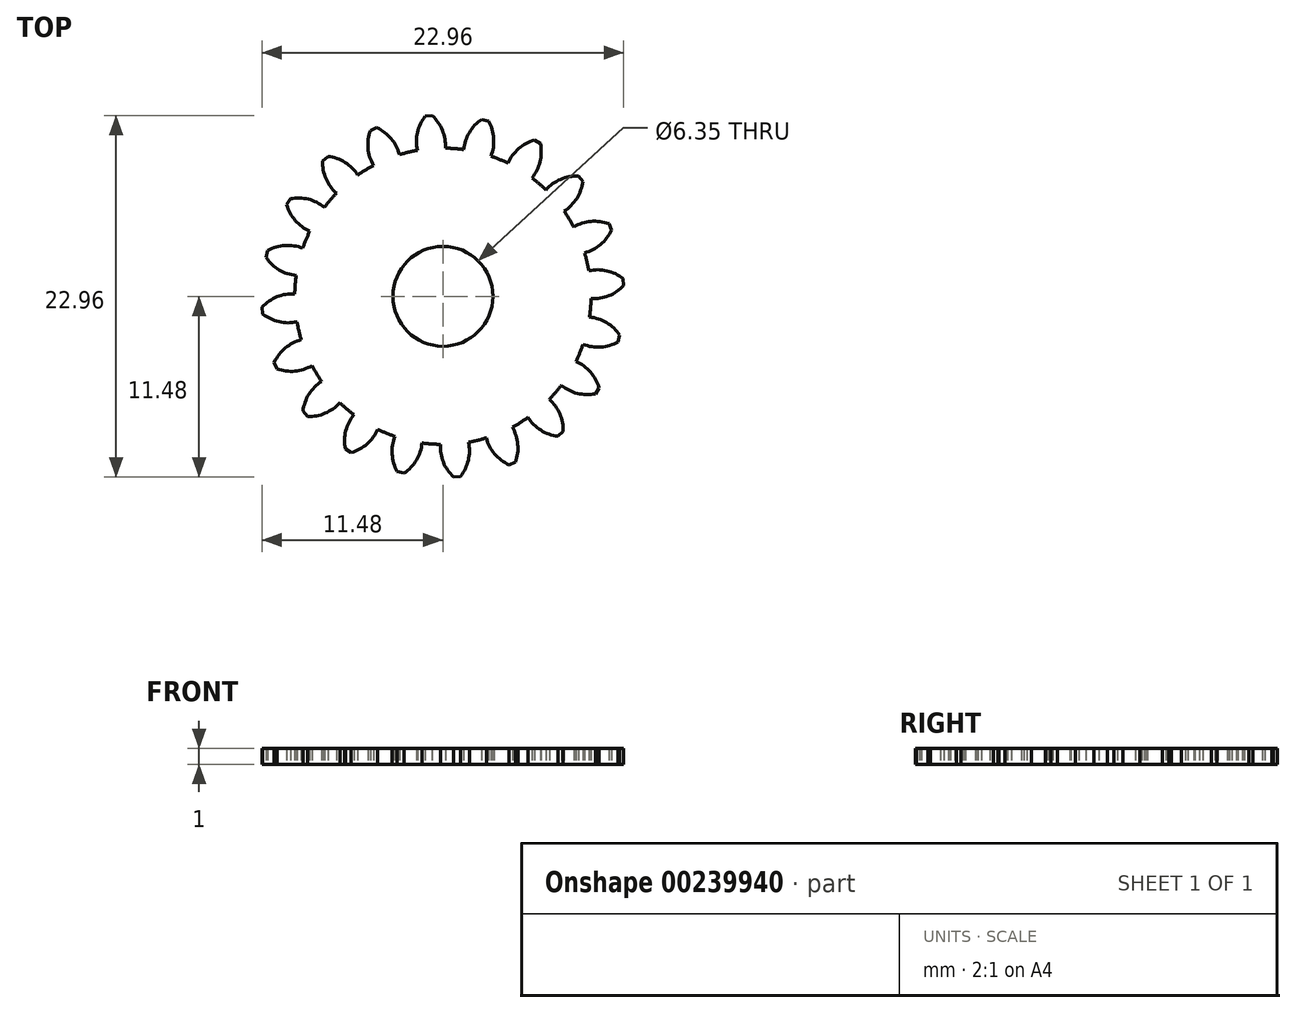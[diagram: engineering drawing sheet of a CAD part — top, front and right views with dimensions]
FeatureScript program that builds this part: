
annotation { "Feature Type Name" : "Feature", "Feature Type Description" : "" }
export const myFeature = defineFeature(function(context is Context, id is Id, definition is map)
    precondition{}
    {
        {
            assignVariable(context, id + "F0", {"name" : "GearDepth", "anyValue" : 1});
        }
        {
            var Q0;
            Q0=qCreatedBy(makeId("Top.planeOp"),FACE);
            var sketch = newSketch(context, id + "F1", { "sketchPlane" : qUnion([Q0])});
            skCircle(sketch, "E0", {"center": v(0, 0) * mm, "radius": 9.4 * mm});
            skCircle(sketch, "E1", {"center": v(0, 0) * mm, "radius": 10.45 * mm, "construction": true});
            skCircle(sketch, "E2", {"center": v(0, 0) * mm, "radius": 11.5 * mm, "construction": true});
            skLineSegment(sketch, "E3", {"start": v(0, 0) * mm, "end": v(0, 17.6) * mm, "construction": true});
            skLineSegment(sketch, "E4", {"start": v(0, 0) * mm, "end": v(-1.42, 18) * mm, "construction": true});
            skLineSegment(sketch, "E5", {"start": v(0, 10.45) * mm, "end": v(-10.54, 10.45) * mm, "construction": true});
            skLineSegment(sketch, "E6", {"start": v(0, 10.45) * mm, "end": v(-10.3, 6.7) * mm, "construction": true});
            skCircle(sketch, "E7", {"center": v(0, 10.45) * mm, "radius": 2.61 * mm, "construction": true});
            skCircle(sketch, "E8", {"center": v(-2.46, 9.56) * mm, "radius": 2.61 * mm, "construction": true});
            skArc(sketch, "E9", {"start": v(-4.91, 10.45) * mm, "mid": v(-4.92, 10.42) * mm, "end": v(-4.94, 10.39) * mm});
            skArc(sketch, "E10.trimOffspring", {"start": v(0.15, 9.4) * mm, "mid": v(-0.03, 10.54) * mm, "end": v(-0.68, 11.48) * mm});
            skArc(sketch, "E11.MirrorCS", {"start": v(-1.62, 9.27) * mm, "mid": v(-1.62, 10.41) * mm, "end": v(-1.12, 11.45) * mm});
            skLineSegment(sketch, "E12", {"start": v(-1.12, 11.45) * mm, "end": v(-0.68, 11.48) * mm});
            skArc(sketch, "E13.1.0", {"start": v(-2.76, 9) * mm, "mid": v(-3.29, 10.01) * mm, "end": v(-4.2, 10.7) * mm});
            skLineSegment(sketch, "E13.1.1", {"start": v(-4.6, 10.54) * mm, "end": v(-4.2, 10.7) * mm});
            skArc(sketch, "E13.1.2", {"start": v(-4.4, 8.31) * mm, "mid": v(-4.76, 9.4) * mm, "end": v(-4.6, 10.54) * mm});
            skArc(sketch, "E13.2.0", {"start": v(-5.4, 7.7) * mm, "mid": v(-6.22, 8.5) * mm, "end": v(-7.3, 8.89) * mm});
            skLineSegment(sketch, "E13.2.1", {"start": v(-7.64, 8.6) * mm, "end": v(-7.3, 8.89) * mm});
            skArc(sketch, "E13.2.2", {"start": v(-6.76, 6.54) * mm, "mid": v(-7.43, 7.47) * mm, "end": v(-7.64, 8.6) * mm});
            skArc(sketch, "E13.3.0", {"start": v(-7.52, 5.65) * mm, "mid": v(-8.54, 6.17) * mm, "end": v(-9.69, 6.2) * mm});
            skLineSegment(sketch, "E13.3.1", {"start": v(-9.92, 5.82) * mm, "end": v(-9.69, 6.2) * mm});
            skArc(sketch, "E13.3.2", {"start": v(-8.45, 4.13) * mm, "mid": v(-9.37, 4.81) * mm, "end": v(-9.92, 5.82) * mm});
            skArc(sketch, "E13.4.0", {"start": v(-8.9, 3.05) * mm, "mid": v(-10.03, 3.23) * mm, "end": v(-11.13, 2.9) * mm});
            skLineSegment(sketch, "E13.4.1", {"start": v(-11.23, 2.47) * mm, "end": v(-11.13, 2.9) * mm});
            skArc(sketch, "E13.4.2", {"start": v(-9.32, 1.32) * mm, "mid": v(-10.4, 1.68) * mm, "end": v(-11.23, 2.47) * mm});
            skArc(sketch, "E13.5.0", {"start": v(-9.4, 0.15) * mm, "mid": v(-10.54, -0.03) * mm, "end": v(-11.48, -0.68) * mm});
            skLineSegment(sketch, "E13.5.1", {"start": v(-11.45, -1.12) * mm, "end": v(-11.48, -0.68) * mm});
            skArc(sketch, "E13.5.2", {"start": v(-9.27, -1.62) * mm, "mid": v(-10.41, -1.62) * mm, "end": v(-11.45, -1.12) * mm});
            skArc(sketch, "E13.6.0", {"start": v(-9, -2.76) * mm, "mid": v(-10.01, -3.29) * mm, "end": v(-10.7, -4.2) * mm});
            skLineSegment(sketch, "E13.6.1", {"start": v(-10.54, -4.6) * mm, "end": v(-10.7, -4.2) * mm});
            skArc(sketch, "E13.6.2", {"start": v(-8.31, -4.4) * mm, "mid": v(-9.4, -4.76) * mm, "end": v(-10.54, -4.6) * mm});
            skArc(sketch, "E13.7.0", {"start": v(-7.7, -5.4) * mm, "mid": v(-8.5, -6.22) * mm, "end": v(-8.89, -7.3) * mm});
            skLineSegment(sketch, "E13.7.1", {"start": v(-8.6, -7.64) * mm, "end": v(-8.89, -7.3) * mm});
            skArc(sketch, "E13.7.2", {"start": v(-6.54, -6.76) * mm, "mid": v(-7.47, -7.43) * mm, "end": v(-8.6, -7.64) * mm});
            skArc(sketch, "E13.8.0", {"start": v(-5.65, -7.52) * mm, "mid": v(-6.17, -8.54) * mm, "end": v(-6.2, -9.69) * mm});
            skLineSegment(sketch, "E13.8.1", {"start": v(-5.82, -9.92) * mm, "end": v(-6.2, -9.69) * mm});
            skArc(sketch, "E13.8.2", {"start": v(-4.13, -8.45) * mm, "mid": v(-4.81, -9.37) * mm, "end": v(-5.82, -9.92) * mm});
            skArc(sketch, "E13.9.0", {"start": v(-3.05, -8.9) * mm, "mid": v(-3.23, -10.03) * mm, "end": v(-2.9, -11.13) * mm});
            skLineSegment(sketch, "E13.9.1", {"start": v(-2.47, -11.23) * mm, "end": v(-2.9, -11.13) * mm});
            skArc(sketch, "E13.9.2", {"start": v(-1.32, -9.32) * mm, "mid": v(-1.68, -10.4) * mm, "end": v(-2.47, -11.23) * mm});
            skArc(sketch, "E13.10.0", {"start": v(-0.15, -9.4) * mm, "mid": v(0.03, -10.54) * mm, "end": v(0.68, -11.48) * mm});
            skLineSegment(sketch, "E13.10.1", {"start": v(1.12, -11.45) * mm, "end": v(0.68, -11.48) * mm});
            skArc(sketch, "E13.10.2", {"start": v(1.62, -9.27) * mm, "mid": v(1.62, -10.41) * mm, "end": v(1.12, -11.45) * mm});
            skArc(sketch, "E13.11.0", {"start": v(2.76, -9) * mm, "mid": v(3.29, -10.01) * mm, "end": v(4.2, -10.7) * mm});
            skLineSegment(sketch, "E13.11.1", {"start": v(4.6, -10.54) * mm, "end": v(4.2, -10.7) * mm});
            skArc(sketch, "E13.11.2", {"start": v(4.4, -8.31) * mm, "mid": v(4.76, -9.4) * mm, "end": v(4.6, -10.54) * mm});
            skArc(sketch, "E13.12.0", {"start": v(5.4, -7.7) * mm, "mid": v(6.22, -8.5) * mm, "end": v(7.3, -8.89) * mm});
            skLineSegment(sketch, "E13.12.1", {"start": v(7.64, -8.6) * mm, "end": v(7.3, -8.89) * mm});
            skArc(sketch, "E13.12.2", {"start": v(6.76, -6.54) * mm, "mid": v(7.43, -7.47) * mm, "end": v(7.64, -8.6) * mm});
            skArc(sketch, "E13.13.0", {"start": v(7.52, -5.65) * mm, "mid": v(8.54, -6.17) * mm, "end": v(9.69, -6.2) * mm});
            skLineSegment(sketch, "E13.13.1", {"start": v(9.92, -5.82) * mm, "end": v(9.69, -6.2) * mm});
            skArc(sketch, "E13.13.2", {"start": v(8.45, -4.13) * mm, "mid": v(9.37, -4.81) * mm, "end": v(9.92, -5.82) * mm});
            skArc(sketch, "E13.14.0", {"start": v(8.9, -3.05) * mm, "mid": v(10.03, -3.23) * mm, "end": v(11.13, -2.9) * mm});
            skLineSegment(sketch, "E13.14.1", {"start": v(11.23, -2.47) * mm, "end": v(11.13, -2.9) * mm});
            skArc(sketch, "E13.14.2", {"start": v(9.32, -1.32) * mm, "mid": v(10.4, -1.68) * mm, "end": v(11.23, -2.47) * mm});
            skArc(sketch, "E13.15.0", {"start": v(9.4, -0.15) * mm, "mid": v(10.54, 0.03) * mm, "end": v(11.48, 0.68) * mm});
            skLineSegment(sketch, "E13.15.1", {"start": v(11.45, 1.12) * mm, "end": v(11.48, 0.68) * mm});
            skArc(sketch, "E13.15.2", {"start": v(9.27, 1.62) * mm, "mid": v(10.41, 1.62) * mm, "end": v(11.45, 1.12) * mm});
            skArc(sketch, "E13.16.0", {"start": v(9, 2.76) * mm, "mid": v(10.01, 3.29) * mm, "end": v(10.7, 4.2) * mm});
            skLineSegment(sketch, "E13.16.1", {"start": v(10.54, 4.6) * mm, "end": v(10.7, 4.2) * mm});
            skArc(sketch, "E13.16.2", {"start": v(8.31, 4.4) * mm, "mid": v(9.4, 4.76) * mm, "end": v(10.54, 4.6) * mm});
            skArc(sketch, "E13.17.0", {"start": v(7.7, 5.4) * mm, "mid": v(8.5, 6.22) * mm, "end": v(8.89, 7.3) * mm});
            skLineSegment(sketch, "E13.17.1", {"start": v(8.6, 7.64) * mm, "end": v(8.89, 7.3) * mm});
            skArc(sketch, "E13.17.2", {"start": v(6.54, 6.76) * mm, "mid": v(7.47, 7.43) * mm, "end": v(8.6, 7.64) * mm});
            skArc(sketch, "E13.18.0", {"start": v(5.65, 7.52) * mm, "mid": v(6.17, 8.54) * mm, "end": v(6.2, 9.69) * mm});
            skLineSegment(sketch, "E13.18.1", {"start": v(5.82, 9.92) * mm, "end": v(6.2, 9.69) * mm});
            skArc(sketch, "E13.18.2", {"start": v(4.13, 8.45) * mm, "mid": v(4.81, 9.37) * mm, "end": v(5.82, 9.92) * mm});
            skArc(sketch, "E13.19.0", {"start": v(3.05, 8.9) * mm, "mid": v(3.23, 10.03) * mm, "end": v(2.9, 11.13) * mm});
            skLineSegment(sketch, "E13.19.1", {"start": v(2.47, 11.23) * mm, "end": v(2.9, 11.13) * mm});
            skArc(sketch, "E13.19.2", {"start": v(1.32, 9.32) * mm, "mid": v(1.68, 10.4) * mm, "end": v(2.47, 11.23) * mm});
            skCircle(sketch, "E14", {"center": v(0, 0) * mm, "radius": 3.17 * mm});
            skSolve(sketch);
        }
        {
            var Q0;
            {var subQ0=sQuery(id+"F1.wireOp",EDGE,"E10.trimOffspring");Q0=makeQuery(id+"F1.imprint","IMPRINT",FACE,{"disambiguationData":[TD([[makeQuery(id+"F1.imprint","IMPRINT",EDGE,{"derivedFrom":subQ0}),1.0]])]});}
            var Q1;
            {var subQ0=sQuery(id+"F1.wireOp",EDGE,"E0");var subQ1=makeQuery(id+"F1.imprint","INTERSECT",VERTEX,{"derivedFrom":[subQ0,sQuery(id+"F1.wireOp",EDGE,"E10.trimOffspring")]});Q1=makeQuery(id+"F1.imprint","IMPRINT",FACE,{"disambiguationData":[TD([[makeQuery(id+"F1.imprint","IMPRINT",EDGE,{"disambiguationData":[TD([[subQ1,-1.0]])],"derivedFrom":subQ0}),1.0]])]});}
            var Q2;
            {var subQ0=sQuery(id+"F1.wireOp",EDGE,"E13.1.0");Q2=makeQuery(id+"F1.imprint","IMPRINT",FACE,{"disambiguationData":[TD([[makeQuery(id+"F1.imprint","IMPRINT",EDGE,{"derivedFrom":subQ0}),1.0]])]});}
            var Q3;
            {var subQ0=sQuery(id+"F1.wireOp",EDGE,"E13.2.0");Q3=makeQuery(id+"F1.imprint","IMPRINT",FACE,{"disambiguationData":[TD([[makeQuery(id+"F1.imprint","IMPRINT",EDGE,{"derivedFrom":subQ0}),1.0]])]});}
            var Q4;
            {var subQ0=sQuery(id+"F1.wireOp",EDGE,"E13.3.0");Q4=makeQuery(id+"F1.imprint","IMPRINT",FACE,{"disambiguationData":[TD([[makeQuery(id+"F1.imprint","IMPRINT",EDGE,{"derivedFrom":subQ0}),1.0]])]});}
            var Q5;
            {var subQ0=sQuery(id+"F1.wireOp",EDGE,"E13.4.0");Q5=makeQuery(id+"F1.imprint","IMPRINT",FACE,{"disambiguationData":[TD([[makeQuery(id+"F1.imprint","IMPRINT",EDGE,{"derivedFrom":subQ0}),1.0]])]});}
            var Q6;
            {var subQ0=sQuery(id+"F1.wireOp",EDGE,"E13.5.0");Q6=makeQuery(id+"F1.imprint","IMPRINT",FACE,{"disambiguationData":[TD([[makeQuery(id+"F1.imprint","IMPRINT",EDGE,{"derivedFrom":subQ0}),1.0]])]});}
            var Q7;
            {var subQ0=sQuery(id+"F1.wireOp",EDGE,"E13.6.0");Q7=makeQuery(id+"F1.imprint","IMPRINT",FACE,{"disambiguationData":[TD([[makeQuery(id+"F1.imprint","IMPRINT",EDGE,{"derivedFrom":subQ0}),1.0]])]});}
            var Q8;
            {var subQ0=sQuery(id+"F1.wireOp",EDGE,"E13.7.0");Q8=makeQuery(id+"F1.imprint","IMPRINT",FACE,{"disambiguationData":[TD([[makeQuery(id+"F1.imprint","IMPRINT",EDGE,{"derivedFrom":subQ0}),1.0]])]});}
            var Q9;
            {var subQ0=sQuery(id+"F1.wireOp",EDGE,"E13.8.0");Q9=makeQuery(id+"F1.imprint","IMPRINT",FACE,{"disambiguationData":[TD([[makeQuery(id+"F1.imprint","IMPRINT",EDGE,{"derivedFrom":subQ0}),1.0]])]});}
            var Q10;
            {var subQ0=sQuery(id+"F1.wireOp",EDGE,"E13.9.0");Q10=makeQuery(id+"F1.imprint","IMPRINT",FACE,{"disambiguationData":[TD([[makeQuery(id+"F1.imprint","IMPRINT",EDGE,{"derivedFrom":subQ0}),1.0]])]});}
            var Q11;
            {var subQ0=sQuery(id+"F1.wireOp",EDGE,"E13.10.0");Q11=makeQuery(id+"F1.imprint","IMPRINT",FACE,{"disambiguationData":[TD([[makeQuery(id+"F1.imprint","IMPRINT",EDGE,{"derivedFrom":subQ0}),1.0]])]});}
            var Q12;
            {var subQ0=sQuery(id+"F1.wireOp",EDGE,"E13.11.0");Q12=makeQuery(id+"F1.imprint","IMPRINT",FACE,{"disambiguationData":[TD([[makeQuery(id+"F1.imprint","IMPRINT",EDGE,{"derivedFrom":subQ0}),1.0]])]});}
            var Q13;
            {var subQ0=sQuery(id+"F1.wireOp",EDGE,"E13.12.0");Q13=makeQuery(id+"F1.imprint","IMPRINT",FACE,{"disambiguationData":[TD([[makeQuery(id+"F1.imprint","IMPRINT",EDGE,{"derivedFrom":subQ0}),1.0]])]});}
            var Q14;
            {var subQ0=sQuery(id+"F1.wireOp",EDGE,"E13.13.0");Q14=makeQuery(id+"F1.imprint","IMPRINT",FACE,{"disambiguationData":[TD([[makeQuery(id+"F1.imprint","IMPRINT",EDGE,{"derivedFrom":subQ0}),1.0]])]});}
            var Q15;
            {var subQ0=sQuery(id+"F1.wireOp",EDGE,"E13.14.0");Q15=makeQuery(id+"F1.imprint","IMPRINT",FACE,{"disambiguationData":[TD([[makeQuery(id+"F1.imprint","IMPRINT",EDGE,{"derivedFrom":subQ0}),1.0]])]});}
            var Q16;
            {var subQ0=sQuery(id+"F1.wireOp",EDGE,"E13.15.0");Q16=makeQuery(id+"F1.imprint","IMPRINT",FACE,{"disambiguationData":[TD([[makeQuery(id+"F1.imprint","IMPRINT",EDGE,{"derivedFrom":subQ0}),1.0]])]});}
            var Q17;
            {var subQ0=sQuery(id+"F1.wireOp",EDGE,"E13.16.0");Q17=makeQuery(id+"F1.imprint","IMPRINT",FACE,{"disambiguationData":[TD([[makeQuery(id+"F1.imprint","IMPRINT",EDGE,{"derivedFrom":subQ0}),1.0]])]});}
            var Q18;
            {var subQ0=sQuery(id+"F1.wireOp",EDGE,"E13.17.0");Q18=makeQuery(id+"F1.imprint","IMPRINT",FACE,{"disambiguationData":[TD([[makeQuery(id+"F1.imprint","IMPRINT",EDGE,{"derivedFrom":subQ0}),1.0]])]});}
            var Q19;
            {var subQ0=sQuery(id+"F1.wireOp",EDGE,"E13.18.0");Q19=makeQuery(id+"F1.imprint","IMPRINT",FACE,{"disambiguationData":[TD([[makeQuery(id+"F1.imprint","IMPRINT",EDGE,{"derivedFrom":subQ0}),1.0]])]});}
            var Q20;
            {var subQ0=sQuery(id+"F1.wireOp",EDGE,"E13.19.0");Q20=makeQuery(id+"F1.imprint","IMPRINT",FACE,{"disambiguationData":[TD([[makeQuery(id+"F1.imprint","IMPRINT",EDGE,{"derivedFrom":subQ0}),1.0]])]});}
            var Q21;
            Q21=sQuery(id+"F1.wireOp",EDGE,"E0");
            var Q22;
            Q22=sQuery(id+"F1.wireOp",EDGE,"E10.trimOffspring");
            var Q23;
            Q23=sQuery(id+"F1.wireOp",EDGE,"E12");
            var Q24;
            Q24=sQuery(id+"F1.wireOp",EDGE,"E11.MirrorCS");
            extrude(context, id + "F2", {"entities" : qUnion([Q0, Q1, Q2, Q3, Q4, Q5, Q6, Q7, Q8, Q9, Q10, Q11, Q12, Q13, Q14, Q15, Q16, Q17, Q18, Q19, Q20]), "surfaceEntities" : qUnion([Q21, Q22, Q23, Q24]), "depth" : (getVariable(context, 'GearDepth')) * mm});
        }
    });
